# Revit family: Gira_511000
name_source: partatom
category: Elektroinstallationen
revit_build: Autodesk Revit 2017 (Build: 20160225_1515(x64)
units: mm (PartAtom-declared; Revit-internal decimal feet)

## family parameters
Basisbauteil = Fläche
Beim Laden mit Abzugskörper schneiden = Nein
Bemaßung runder Anschluss = Durchmesser verwenden
Beschriftungsausrichtung beibehalten = Nein
Gemeinsam genutzt = Nein
Raumberechnungspunkt = Nein
Teiletyp = Normal

## types (1)
- Gira_511000
    BIM = https://media.stage.bim.site
    Beschreibung = RF TP Media coupl.RF rep. KNX,KNX RF TP media coupler or RF repeater,,DRA plus,With the KNX RF system devices, the KNX RF pushbutton sensors and KNX RF hand-held transmitters are incorporated and parameterised in the KNX structure via the ETS.,,Features:,- Interface between wired KNX products (TP) and KNX RF wireless products.,- Configurable as a media coupler or repeater via the ETS.,- Project planning, start-up and parameter setting are performed using ETS (version 5 or later).
    Data sheet = https://katalog.gira.de
    GTIN = 4010337017264
    HAN = 511000
    Hersteller = Gira
    Productwebsite = http://katalog.gira.de
    Type of accessory = Other
    Typname = RF/TP media coup./RF repeater KNX
    URL = https://www.gira.de
    Vorgabe-Ansicht = 1219 mm

## geometry (parser evidence)
native form markers: Sweep x2
no freeform markers — native parametric forms only
